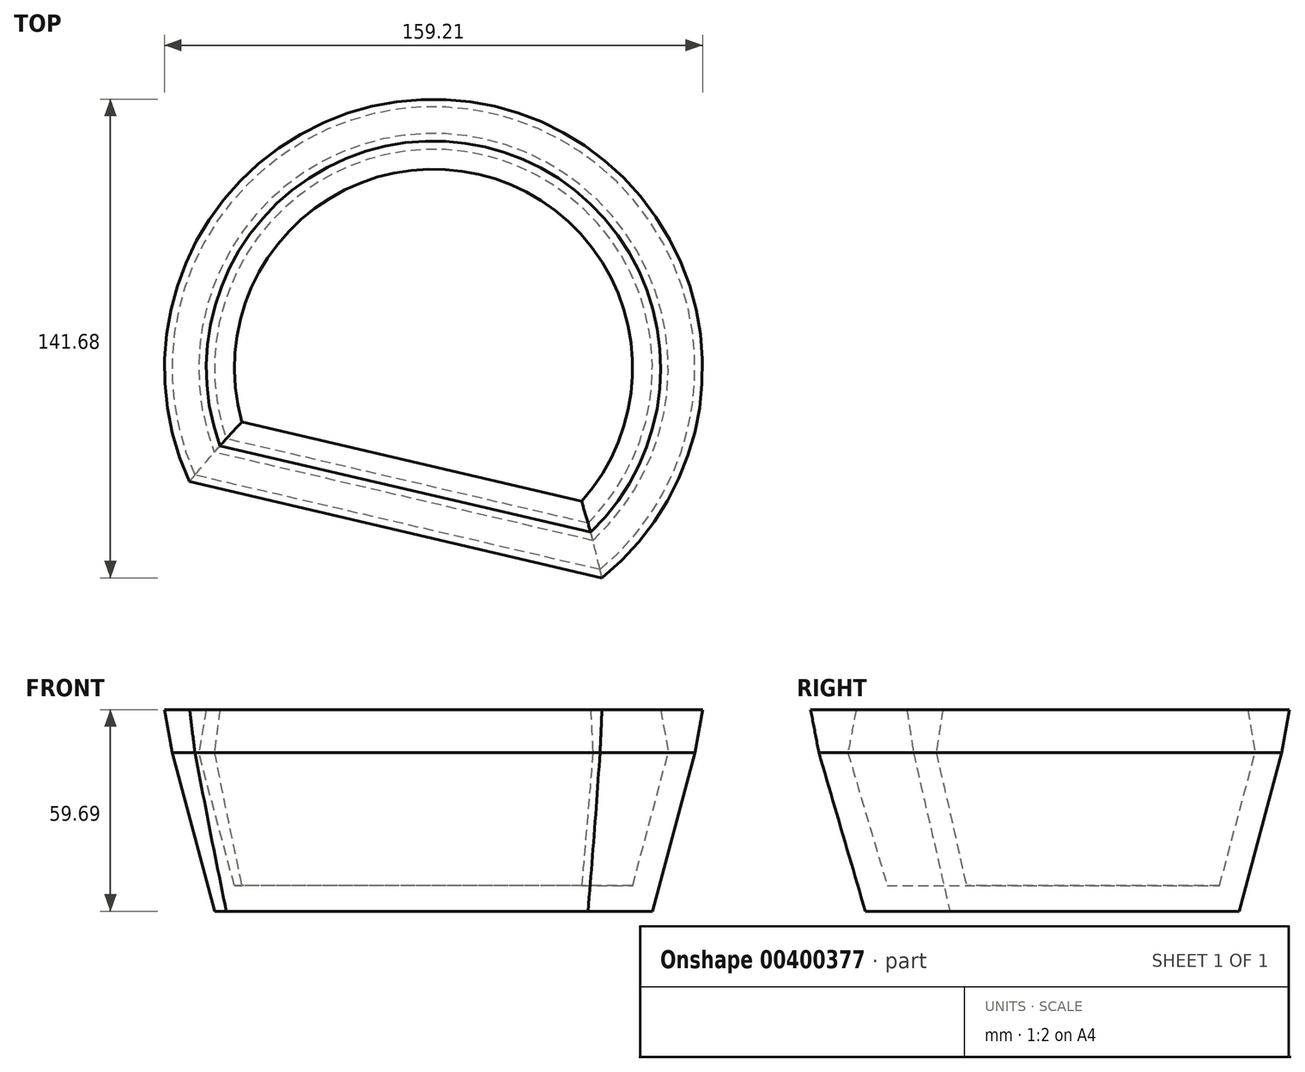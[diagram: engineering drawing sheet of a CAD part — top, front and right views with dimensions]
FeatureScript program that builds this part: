
annotation { "Feature Type Name" : "Feature", "Feature Type Description" : "" }
export const myFeature = defineFeature(function(context is Context, id is Id, definition is map)
    precondition{}
    {
        {
            var Q0;
            Q0=qCreatedBy(makeId("Top.planeOp"),FACE);
            var sketch = newSketch(context, id + "F0", { "sketchPlane" : qUnion([Q0])});
            skArc(sketch, "E0", {"start": v(-76.28, 0) * mm, "mid": v(-107.3, 108.96) * mm, "end": v(-183.33, 24.98) * mm});
            skLineSegment(sketch, "E1", {"start": v(-183.33, 24.98) * mm, "end": v(-76.28, 0) * mm});
            skSolve(sketch);
        }
        {
            var Q0;
            Q0=makeQuery(id+"F0.imprint","IMPRINT",FACE,{"disambiguationData":[TD([[makeQuery(id+"F0.imprint","IMPRINT",EDGE,{"derivedFrom":sQuery(id+"F0.wireOp",EDGE,"E0")}),1.0]])]});
            extrude(context, id + "F1", {"entities" : qUnion([Q0]), "depth" : 47 * mm, "hasDraft" : true, "draftAngle" : 15 * degree});
        }
        {
            var Q0;
            Q0=makeQuery(id+"F1.opExtrude","CAP_FACE",FACE,{"disambiguationData":[OSD([sQuery(id+"F0.wireOp",EDGE,"E0")])],"isStart":false});
            shell(context, id + "F2", {"entities" : qUnion([Q0]), "thickness" : 7.62 * mm});
        }
        {
            var Q0;
            Q0=makeQuery(id+"F1.opExtrude","CAP_FACE",FACE,{"disambiguationData":[OSD([sQuery(id+"F0.wireOp",EDGE,"E0"),sQuery(id+"F0.wireOp",EDGE,"E1")])],"isStart":false});
            extrude(context, id + "F3", {"entities" : qUnion([Q0]), "operationType" : NewBodyOperationType.ADD, "depth" : 12.7 * mm, "hasDraft" : true, "draftAngle" : 10 * degree});
        }
    });
